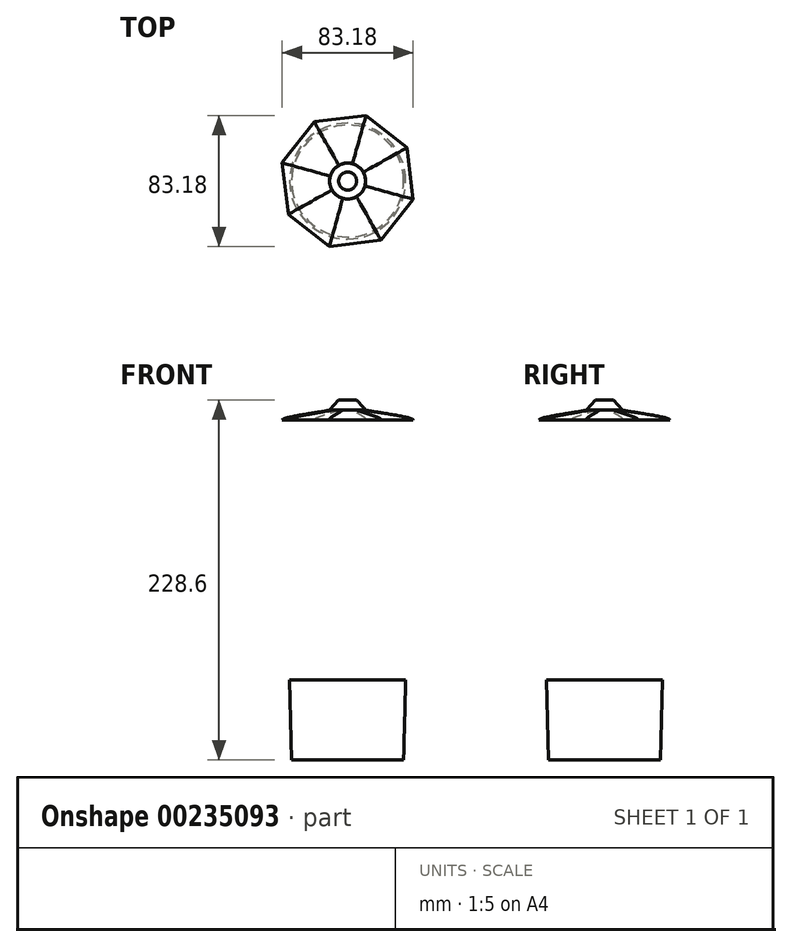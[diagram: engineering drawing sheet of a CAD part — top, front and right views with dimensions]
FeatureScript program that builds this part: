
annotation { "Feature Type Name" : "Feature", "Feature Type Description" : "" }
export const myFeature = defineFeature(function(context is Context, id is Id, definition is map)
    precondition{}
    {
        {
            var Q0;
            Q0=qCreatedBy(makeId("Top.planeOp"),FACE);
            cPlane(context, id + "F0", {"entities" : qUnion([Q0]), "cplaneType" : CPlaneType.OFFSET, "offset" : 12.7 * mm, "width" : 152.4 * mm, "height" : 152.4 * mm});
        }
        {
            var Q0;
            Q0=qCreatedBy(makeId("Top.planeOp"),FACE);
            cPlane(context, id + "F1", {"entities" : qUnion([Q0]), "cplaneType" : CPlaneType.OFFSET, "offset" : 12.7 * mm, "oppositeDirection" : true, "width" : 152.4 * mm, "height" : 152.4 * mm});
        }
        {
            var Q0;
            Q0=qCreatedBy(makeId("Top.planeOp"),FACE);
            cPlane(context, id + "F2", {"entities" : qUnion([Q0]), "cplaneType" : CPlaneType.OFFSET, "offset" : 215.9 * mm, "oppositeDirection" : true, "width" : 152.4 * mm, "height" : 152.4 * mm});
        }
        {
            var Q0;
            Q0=qCreatedBy(id+"F1.planeOp",FACE);
            cPlane(context, id + "F3", {"entities" : qUnion([Q0]), "cplaneType" : CPlaneType.OFFSET, "offset" : 152.4 * mm, "oppositeDirection" : true, "width" : 152.4 * mm, "height" : 152.4 * mm});
        }
        {
            var Q0;
            Q0=qCreatedBy(id+"F2.planeOp",FACE);
            var sketch = newSketch(context, id + "F4", { "sketchPlane" : qUnion([Q0])});
            skCircle(sketch, "E0", {"center": v(0, 0) * mm, "radius": 35.56 * mm});
            skSolve(sketch);
        }
        {
            var Q0;
            Q0=qCreatedBy(id+"F3.planeOp",FACE);
            var sketch = newSketch(context, id + "F5", { "sketchPlane" : qUnion([Q0])});
            skCircle(sketch, "E1", {"center": v(0, 0) * mm, "radius": 36.83 * mm});
            skSolve(sketch);
        }
        {
            var Q0;
            Q0=qCreatedBy(id+"F1.planeOp",FACE);
            var sketch = newSketch(context, id + "F6", { "sketchPlane" : qUnion([Q0])});
            skCircle(sketch, "E2.cCircle", {"center": v(0, 0) * mm, "radius": 43.18 * mm, "construction": true});
            skLineSegment(sketch, "E2.0", {"start": v(21.19, -37.62) * mm, "end": v(-11.62, -41.59) * mm});
            skLineSegment(sketch, "E2.1", {"start": v(-11.62, -41.59) * mm, "end": v(-37.62, -21.19) * mm});
            skLineSegment(sketch, "E2.2", {"start": v(-37.62, -21.19) * mm, "end": v(-41.59, 11.62) * mm});
            skLineSegment(sketch, "E2.3", {"start": v(-41.59, 11.62) * mm, "end": v(-21.19, 37.62) * mm});
            skLineSegment(sketch, "E2.4", {"start": v(-21.19, 37.62) * mm, "end": v(11.62, 41.59) * mm});
            skLineSegment(sketch, "E2.5", {"start": v(11.62, 41.59) * mm, "end": v(37.62, 21.19) * mm});
            skLineSegment(sketch, "E2.6", {"start": v(37.62, 21.19) * mm, "end": v(41.59, -11.62) * mm});
            skLineSegment(sketch, "E2.7", {"start": v(41.59, -11.62) * mm, "end": v(21.19, -37.62) * mm});
            skSolve(sketch);
        }
        {
            var Q0;
            Q0=qCreatedBy(makeId("Top.planeOp"),FACE);
            var sketch = newSketch(context, id + "F7", { "sketchPlane" : qUnion([Q0])});
            skCircle(sketch, "E3.cCircle", {"center": v(0, 0) * mm, "radius": 43.18 * mm, "construction": true});
            skLineSegment(sketch, "E3.0", {"start": v(21.19, -37.62) * mm, "end": v(-11.62, -41.59) * mm});
            skLineSegment(sketch, "E3.1", {"start": v(-11.62, -41.59) * mm, "end": v(-37.62, -21.19) * mm});
            skLineSegment(sketch, "E3.2", {"start": v(-37.62, -21.19) * mm, "end": v(-41.59, 11.62) * mm});
            skLineSegment(sketch, "E3.3", {"start": v(-41.59, 11.62) * mm, "end": v(-21.19, 37.62) * mm});
            skLineSegment(sketch, "E3.4", {"start": v(-21.19, 37.62) * mm, "end": v(11.62, 41.59) * mm});
            skLineSegment(sketch, "E3.5", {"start": v(11.62, 41.59) * mm, "end": v(37.62, 21.19) * mm});
            skLineSegment(sketch, "E3.6", {"start": v(37.62, 21.19) * mm, "end": v(41.59, -11.62) * mm});
            skLineSegment(sketch, "E3.7", {"start": v(41.59, -11.62) * mm, "end": v(21.19, -37.62) * mm});
            skSolve(sketch);
        }
        {
            var Q0;
            Q0=qCreatedBy(id+"F0.planeOp",FACE);
            var sketch = newSketch(context, id + "F8", { "sketchPlane" : qUnion([Q0])});
            skCircle(sketch, "E4", {"center": v(0, 0) * mm, "radius": 5.72 * mm});
            skSolve(sketch);
        }
        {
            var Q0;
            Q0=makeQuery(id+"F6.imprint","IMPRINT",FACE,{"disambiguationData":[TD([[makeQuery(id+"F6.imprint","IMPRINT",EDGE,{"derivedFrom":sQuery(id+"F6.wireOp",EDGE,"E2.0")}),-1.0]])]});
            var Q1;
            Q1=makeQuery(id+"F7.imprint","IMPRINT",FACE,{"disambiguationData":[TD([[makeQuery(id+"F7.imprint","IMPRINT",EDGE,{"derivedFrom":sQuery(id+"F7.wireOp",EDGE,"E3.0")}),-1.0]])]});
            var Q2;
            Q2=makeQuery(id+"F6.imprint","IMPRINT",FACE,{"disambiguationData":[TD([[makeQuery(id+"F6.imprint","IMPRINT",EDGE,{"derivedFrom":sQuery(id+"F6.wireOp",EDGE,"E2.0")}),-1.0]])]});
            var Q3;
            Q3=makeQuery(id+"F7.imprint","IMPRINT",FACE,{"disambiguationData":[TD([[makeQuery(id+"F7.imprint","IMPRINT",EDGE,{"derivedFrom":sQuery(id+"F7.wireOp",EDGE,"E3.0")}),-1.0]])]});
            loft(context, id + "F9", {"bodyType" : ToolBodyType.SURFACE, "sheetProfilesArray" : [{ "sheetProfileEntities" : qUnion([Q0]) }, { "sheetProfileEntities" : qUnion([Q1]) }], "wireProfilesArray" : [{ "wireProfileEntities" : qUnion([Q2]) }, { "wireProfileEntities" : qUnion([Q3]) }]});
        }
        {
            var Q0;
            Q0 = qConstructionFilter(qBodyType(qCreatedBy(id + "F5" ,EDGE), BodyType.WIRE), ConstructionObject.NO);
            var Q1;
            Q1 = qConstructionFilter(qBodyType(qCreatedBy(id + "F6" ,EDGE), BodyType.WIRE), ConstructionObject.NO);
            loft(context, id + "F10", {"bodyType" : ToolBodyType.SURFACE, "startCondition" : LoftEndDerivativeType.NORMAL_TO_PROFILE, "startMagnitude" : 3, "endCondition" : LoftEndDerivativeType.TANGENT_TO_PROFILE, "endMagnitude" : .5, "wireProfilesArray" : [{ "wireProfileEntities" : qUnion([Q0]) }, { "wireProfileEntities" : qUnion([Q1]) }]});
        }
        {
            var Q0;
            Q0=makeQuery(id+"F4.imprint","IMPRINT",FACE,{"disambiguationData":[TD([[makeQuery(id+"F4.imprint","IMPRINT",EDGE,{"derivedFrom":sQuery(id+"F4.wireOp",EDGE,"E0")}),1.0]])]});
            var Q1;
            Q1 = qSketchRegion(id + "F5", true);
            loft(context, id + "F11", {"sheetProfilesArray" : [{ "sheetProfileEntities" : qUnion([Q0]) }, { "sheetProfileEntities" : qUnion([Q1]) }]});
        }
        {
            var Q0;
            Q0=qCreatedBy(makeId("Top.planeOp"),FACE);
            cPlane(context, id + "F12", {"entities" : qUnion([Q0]), "cplaneType" : CPlaneType.OFFSET, "offset" : 6.35 * mm, "width" : 152.4 * mm, "height" : 152.4 * mm});
        }
        {
            var Q0;
            Q0=qCreatedBy(id+"F12.planeOp",FACE);
            var sketch = newSketch(context, id + "F13", { "sketchPlane" : qUnion([Q0])});
            skCircle(sketch, "E5", {"center": v(0, 0) * mm, "radius": 11.43 * mm});
            skSolve(sketch);
        }
        {
            var Q0;
            Q0 = qSketchRegion(id + "F7", true);
            var Q1;
            Q1 = qSketchRegion(id + "F13", true);
            loft(context, id + "F14", {"startCondition" : LoftEndDerivativeType.NORMAL_TO_PROFILE, "startMagnitude" : .75, "endCondition" : LoftEndDerivativeType.NORMAL_TO_PROFILE, "endMagnitude" : .2, "sheetProfilesArray" : [{ "sheetProfileEntities" : qUnion([Q0]) }, { "sheetProfileEntities" : qUnion([Q1]) }]});
        }
        {
            var Q0;
            Q0 = qSketchRegion(id + "F13", true);
            var Q1;
            Q1 = qSketchRegion(id + "F8", true);
            loft(context, id + "F15", {"sheetProfilesArray" : [{ "sheetProfileEntities" : qUnion([Q0]) }, { "sheetProfileEntities" : qUnion([Q1]) }]});
        }
    });
